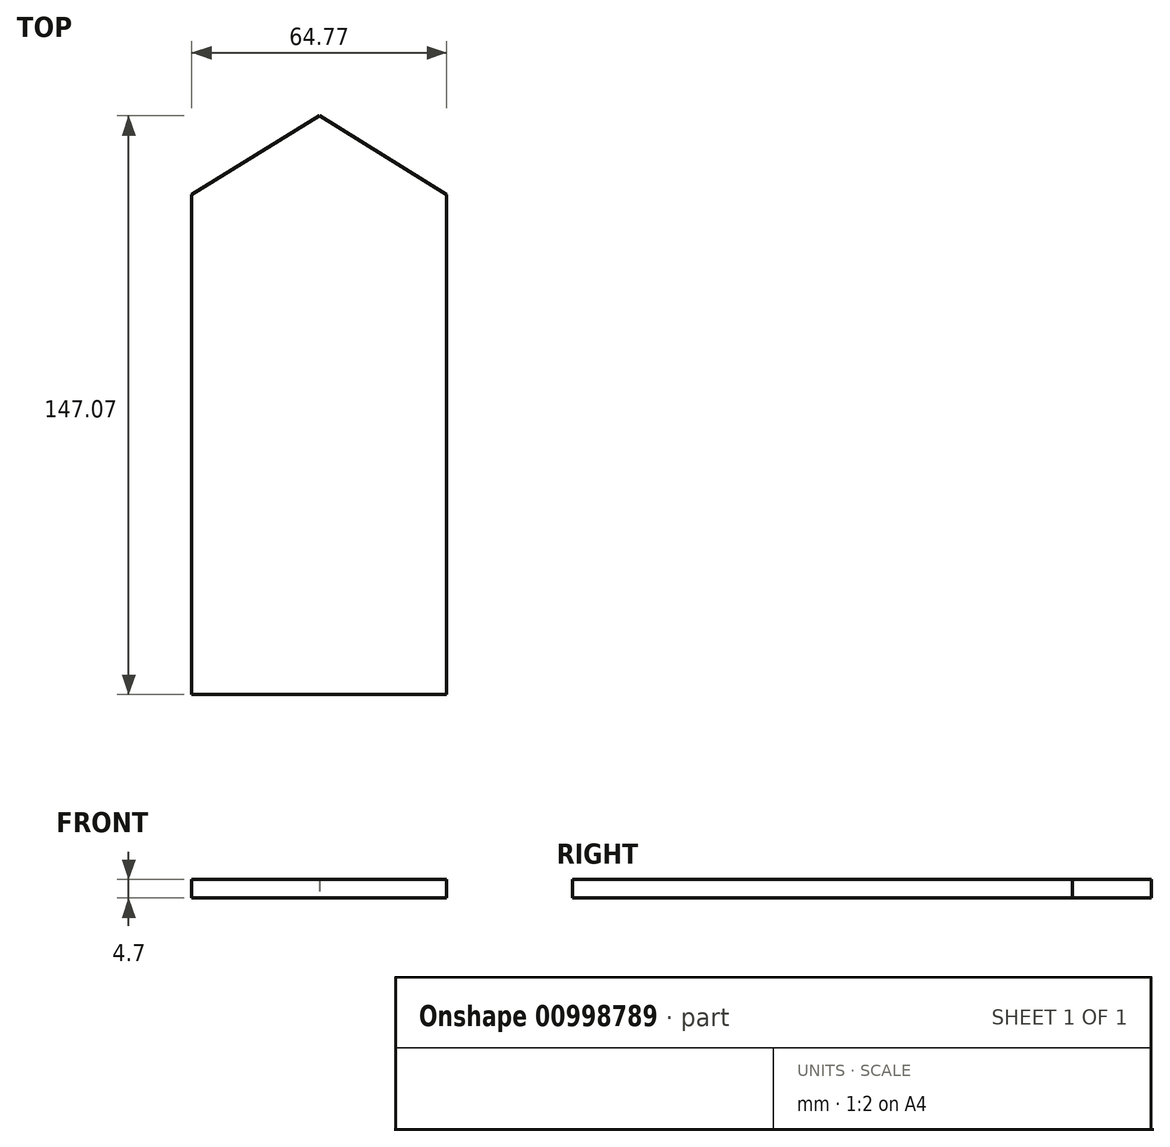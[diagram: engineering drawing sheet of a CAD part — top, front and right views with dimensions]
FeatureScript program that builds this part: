
annotation { "Feature Type Name" : "Feature", "Feature Type Description" : "" }
export const myFeature = defineFeature(function(context is Context, id is Id, definition is map)
    precondition{}
    {
        {
            var Q0;
            Q0=qCreatedBy(makeId("Top.planeOp"),FACE);
            var sketch = newSketch(context, id + "F0", { "sketchPlane" : qUnion([Q0])});
            skLineSegment(sketch, "E0.bottom", {"start": v(32.39, -63.5) * mm, "end": v(-32.38, -63.5) * mm});
            skLineSegment(sketch, "E0.top", {"start": v(32.38, 63.5) * mm, "end": v(-32.39, 63.5) * mm});
            skLineSegment(sketch, "E0.left", {"start": v(32.39, -63.5) * mm, "end": v(32.38, 63.5) * mm});
            skLineSegment(sketch, "E0.right", {"start": v(-32.38, -63.5) * mm, "end": v(-32.39, 63.5) * mm});
            skPoint(sketch, "E0.middle", {"position": v(0, 0) * mm});
            skLineSegment(sketch, "E1", {"start": v(-32.39, 63.5) * mm, "end": v(0, 83.57) * mm});
            skLineSegment(sketch, "E2", {"start": v(0, 83.57) * mm, "end": v(32.38, 63.5) * mm});
            skSolve(sketch);
        }
        {
            var Q0;
            Q0=makeQuery(id+"F0.imprint","IMPRINT",FACE,{"disambiguationData":[TD([[makeQuery(id+"F0.imprint","IMPRINT",EDGE,{"derivedFrom":sQuery(id+"F0.wireOp",EDGE,"E0.bottom")}),-1.0]])]});
            var Q1;
            Q1=makeQuery(id+"F0.imprint","IMPRINT",FACE,{"disambiguationData":[TD([[makeQuery(id+"F0.imprint","IMPRINT",EDGE,{"derivedFrom":sQuery(id+"F0.wireOp",EDGE,"E0.top")}),-1.0]])]});
            extrude(context, id + "F1", {"entities" : qUnion([Q0, Q1]), "depth" : 4.7 * mm, "offsetDistance" : 25.4 * mm});
        }
    });
